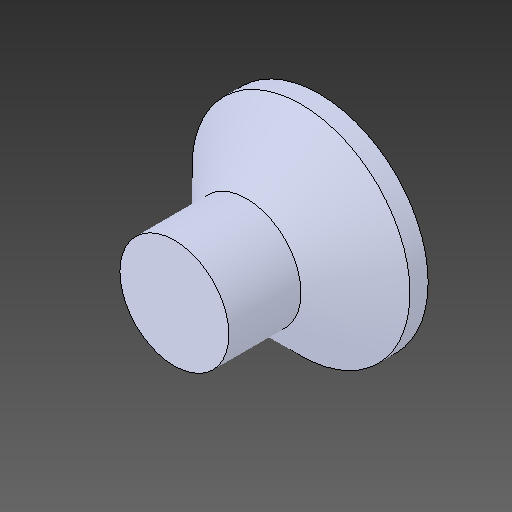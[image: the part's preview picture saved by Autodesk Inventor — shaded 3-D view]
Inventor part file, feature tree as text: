
AUTODESK INVENTOR PART (.ipt)
format: ipt  version: 2018.2 (Build 222227000, 227)  size: 116,736 bytes
history: native  units: mm
features: other x1, chamfer x1
ambient origin geometry x8: Origin, YZ Plane, XZ Plane, XY Plane, X Axis, Y Axis, Z Axis, Center Point
bodies: Body1 (feature_tree)
feature tree (2):
  other  "ソリッド1"
  chamfer  "Chamfer1"  [1 undecoded]
note: 1 required parameter value undecoded (feature->parameter linkage not recoverable at this tier; creation-order binding heuristic only, values carry confidence <= 0.55)
